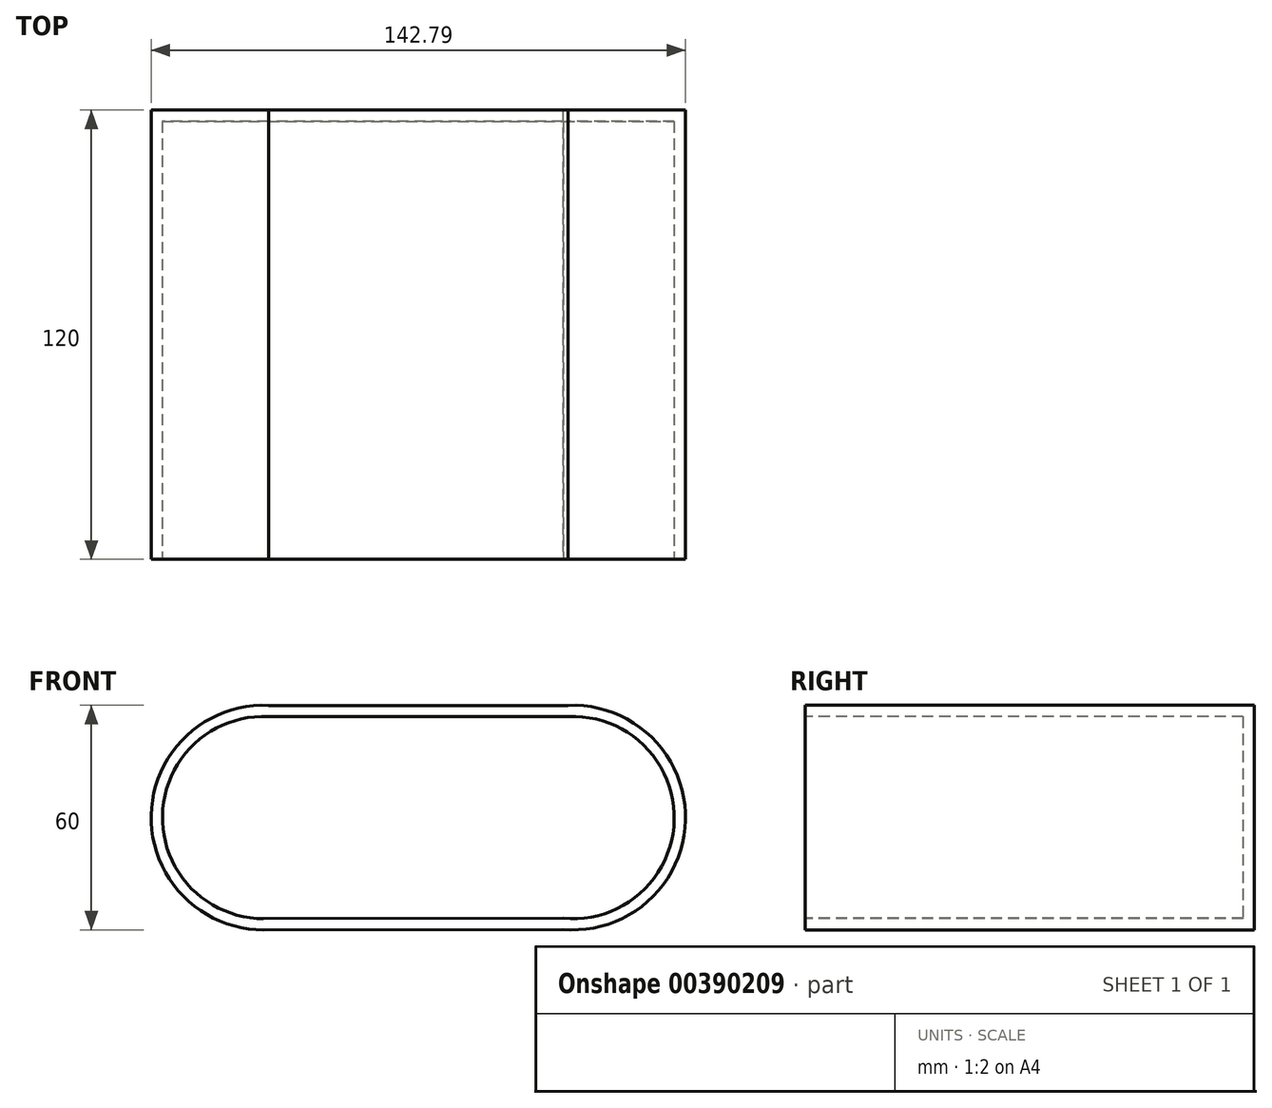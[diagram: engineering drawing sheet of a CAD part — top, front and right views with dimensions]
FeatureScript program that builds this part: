
annotation { "Feature Type Name" : "Feature", "Feature Type Description" : "" }
export const myFeature = defineFeature(function(context is Context, id is Id, definition is map)
    precondition{}
    {
        {
            var Q0;
            Q0=qCreatedBy(makeId("Front.planeOp"),FACE);
            var sketch = newSketch(context, id + "F0", { "sketchPlane" : qUnion([Q0])});
            skArc(sketch, "E0", {"start": v(-36.2, 29.97) * mm, "mid": v(-67.55, 0.65) * mm, "end": v(-37.5, -30) * mm});
            skArc(sketch, "E1", {"start": v(42.44, -29.87) * mm, "mid": v(75.22, -0.72) * mm, "end": v(43.88, 29.97) * mm});
            skLineSegment(sketch, "E2", {"start": v(-38.9, 29.97) * mm, "end": v(43.88, 29.97) * mm});
            skLineSegment(sketch, "E3", {"start": v(48.11, -29.86) * mm, "end": v(-37.5, -30) * mm});
            skLineSegment(sketch, "E4.0", {"start": v(-38.9, 26.97) * mm, "end": v(43.88, 26.97) * mm});
            skArc(sketch, "E5.0", {"start": v(42.72, -26.88) * mm, "mid": v(72.22, -0.65) * mm, "end": v(44.01, 26.97) * mm});
            skLineSegment(sketch, "E6.0", {"start": v(48.1, -26.86) * mm, "end": v(-37.51, -27) * mm});
            skArc(sketch, "E7.0", {"start": v(-36.34, 26.97) * mm, "mid": v(-64.55, 0.58) * mm, "end": v(-37.51, -27) * mm});
            skSolve(sketch);
        }
        {
            var Q0;
            Q0 = qSketchRegion(id + "F0", true);
            extrude(context, id + "F1", {"entities" : qUnion([Q0]), "oppositeDirection" : true, "depth" : 120 * mm});
        }
        {
            var Q0;
            Q0=makeQuery(id+"F1.opExtrude","CAP_FACE",FACE,{"disambiguationData":[OSD([sQuery(id+"F0.wireOp",EDGE,"E0"),sQuery(id+"F0.wireOp",EDGE,"E1"),sQuery(id+"F0.wireOp",EDGE,"E2"),sQuery(id+"F0.wireOp",EDGE,"E3")])],"isStart":true});
            shell(context, id + "F2", {"entities" : qUnion([Q0]), "thickness" : 3 * mm});
        }
    });
